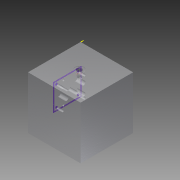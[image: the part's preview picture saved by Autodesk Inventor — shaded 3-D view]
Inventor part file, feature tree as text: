
AUTODESK INVENTOR PART (.ipt)
format: ipt  version: 2014 (Build 180170000, 170)  size: 254,464 bytes
history: native  units: mm
features: other x50, sketch x3, extrude x1
ambient origin geometry x8: Origin, YZ Plane, XZ Plane, XY Plane, X Axis, Y Axis, Z Axis, Center Point
bodies: 实体1 (feature_tree)
feature tree (54):
  extrude  "拉伸1"  TaperAngle=0.0deg  [1 undecoded]
  other  "UCS1"
  other  "UCS2"
  other  "UCS3"
  other  "UCS4"
  other  "UCS5"
  other  "UCS6"
  other  "iFeature4:2"
  other  "iFeature6:1"
  sketch  "草图1"  dims[d0=200.0mm d1=0.0mm]
  other  "UCS1: YZ 平面"
  other  "UCS1: XZ 平面"
  other  "UCS1: XY 平面"
  other  "UCS1: X 轴"
  other  "UCS1: Y 轴"
  other  "UCS1: Z 轴"
  other  "UCS1: 原点"
  other  "UCS2: YZ 平面"
  other  "UCS2: XZ 平面"
  other  "UCS2: XY 平面"
  other  "UCS2: X 轴"
  other  "UCS2: Y 轴"
  other  "UCS2: Z 轴"
  other  "UCS2: 原点"
  other  "UCS3: YZ 平面"
  other  "UCS3: XZ 平面"
  other  "UCS3: XY 平面"
  other  "UCS3: X 轴"
  other  "UCS3: Y 轴"
  other  "UCS3: Z 轴"
  other  "UCS3: 原点"
  other  "UCS4: YZ 平面"
  other  "UCS4: XZ 平面"
  other  "UCS4: XY 平面"
  other  "UCS4: X 轴"
  other  "UCS4: Y 轴"
  other  "UCS4: Z 轴"
  other  "UCS4: 原点"
  other  "UCS5: YZ 平面"
  other  "UCS5: XZ 平面"
  other  "UCS5: XY 平面"
  other  "UCS5: X 轴"
  other  "UCS5: Y 轴"
  other  "UCS5: Z 轴"
  other  "UCS5: 原点"
  other  "UCS6: YZ 平面"
  other  "UCS6: XZ 平面"
  other  "UCS6: XY 平面"
  other  "UCS6: X 轴"
  other  "UCS6: Y 轴"
  other  "UCS6: Z 轴"
  other  "UCS6: 原点"
  sketch  "草图4"  dims[d2=0.0mm d3=0.0mm d4=0.0mm d5=0.0mm d6=0.0mm d7=0.0mm]
  sketch  "草图5"  dims[d8=0.0mm d9=0.0mm d10=0.0mm d11=0.0mm d12=0.0mm d13=0.0mm d14=0.0mm d15=0.0mm d16=0.0mm d17=0.0mm d18=0.0mm d19=0.0mm d20=0.0mm d21=0.0mm d22=0.0mm d23=0.0mm d24=0.0mm d25=0.0mm d26=0.0mm d27=0.0mm d28=0.0mm d29=0.0mm d30=0.0mm d31=0.0mm d32=0.0mm d33=0.0mm d34=0.0mm d35=0.0mm d36=0.0mm d37=0.0mm d38=0.0mm d39=0.0mm d40=0.0mm d41=0.0mm d50=0.0mm d54=-17.0mm d55=0.0mm d59=-17.0mm d60=0.0mm]
note: 1 required parameter value undecoded (feature->parameter linkage not recoverable at this tier; creation-order binding heuristic only, values carry confidence <= 0.55)
